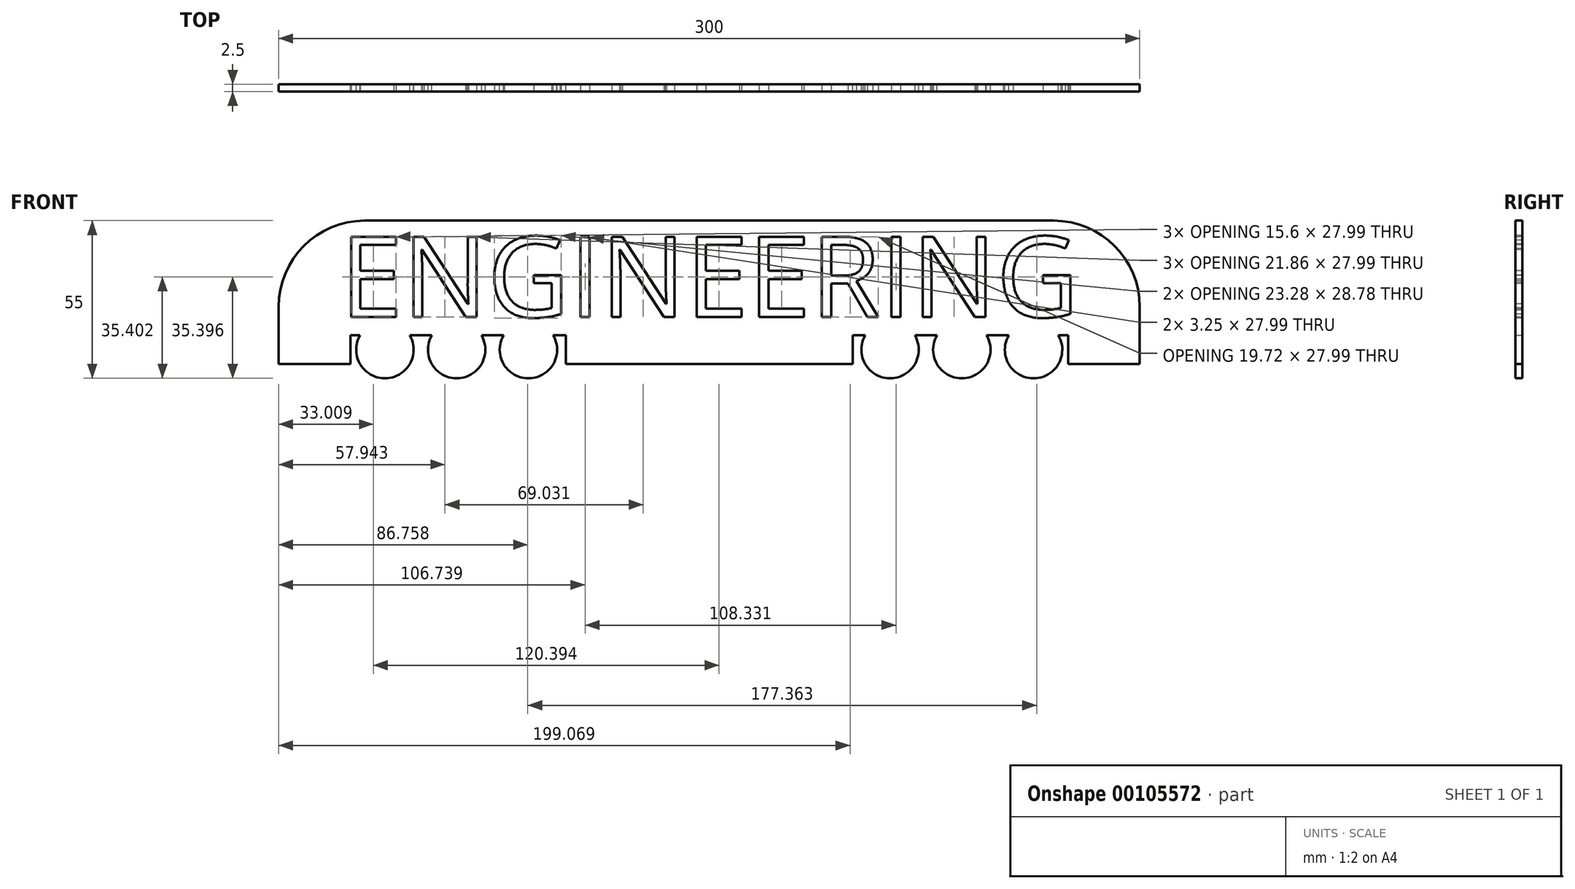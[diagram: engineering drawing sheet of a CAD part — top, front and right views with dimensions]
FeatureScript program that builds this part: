
annotation { "Feature Type Name" : "Feature", "Feature Type Description" : "" }
export const myFeature = defineFeature(function(context is Context, id is Id, definition is map)
    precondition{}
    {
        {
            var Q0;
            Q0=qCreatedBy(makeId("Front.planeOp"),FACE);
            var sketch = newSketch(context, id + "F0", { "sketchPlane" : qUnion([Q0])});
            skLineSegment(sketch, "E0", {"start": v(0, 0) * mm, "end": v(-50, 0) * mm});
            skLineSegment(sketch, "E1", {"start": v(-50, 0) * mm, "end": v(-50, 10) * mm});
            skLineSegment(sketch, "E2", {"start": v(-50, 10) * mm, "end": v(-54.34, 10) * mm});
            skLineSegment(sketch, "E3", {"start": v(-125, 10) * mm, "end": v(-125, 0) * mm});
            skLineSegment(sketch, "E4", {"start": v(-125, 0) * mm, "end": v(-150, 0) * mm});
            skLineSegment(sketch, "E5", {"start": v(-150, 0) * mm, "end": v(-150, 20) * mm});
            skLineSegment(sketch, "E6", {"start": v(-120, 50) * mm, "end": v(0, 50) * mm});
            skLineSegment(sketch, "E7", {"start": v(0, 50) * mm, "end": v(0, 0) * mm, "construction": true});
            skPoint(sketch, "E8.visualSharp", {"position": v(-150, 50) * mm});
            skArc(sketch, "E8.filletArc", {"start": v(-120, 50) * mm, "mid": v(-141.21, 41.21) * mm, "end": v(-150, 20) * mm});
            skArc(sketch, "E9", {"start": v(-121.66, 10) * mm, "mid": v(-113, -5) * mm, "end": v(-104.34, 10) * mm});
            skArc(sketch, "E10.1.0.0", {"start": v(-96.66, 10) * mm, "mid": v(-88, -5) * mm, "end": v(-79.34, 10) * mm});
            skArc(sketch, "E10.2.0.0", {"start": v(-71.66, 10) * mm, "mid": v(-63, -5) * mm, "end": v(-54.34, 10) * mm});
            skLineSegment(sketch, "E10.direction1", {"start": v(-113, 5) * mm, "end": v(-88, 5) * mm, "construction": true});
            skLineSegment(sketch, "E11.trimOffspring", {"start": v(-121.66, 10) * mm, "end": v(-125, 10) * mm});
            skLineSegment(sketch, "E12.trimOffspring", {"start": v(-96.66, 10) * mm, "end": v(-104.34, 10) * mm});
            skLineSegment(sketch, "E13.trimOffspring", {"start": v(-71.66, 10) * mm, "end": v(-79.34, 10) * mm});
            skLineSegment(sketch, "E14.MirrorCS", {"start": v(120, 50) * mm, "end": v(0, 50) * mm});
            skArc(sketch, "E15.MirrorCS", {"start": v(120, 50) * mm, "mid": v(141.21, 41.21) * mm, "end": v(150, 20) * mm});
            skLineSegment(sketch, "E16.MirrorCS", {"start": v(150, 0) * mm, "end": v(150, 20) * mm});
            skLineSegment(sketch, "E17.MirrorCS", {"start": v(125, 0) * mm, "end": v(150, 0) * mm});
            skLineSegment(sketch, "E18.MirrorCS", {"start": v(125, 10) * mm, "end": v(125, 0) * mm});
            skLineSegment(sketch, "E19.MirrorCS", {"start": v(121.66, 10) * mm, "end": v(125, 10) * mm});
            skArc(sketch, "E20.MirrorCS", {"start": v(121.66, 10) * mm, "mid": v(113, -5) * mm, "end": v(104.34, 10) * mm});
            skLineSegment(sketch, "E21.MirrorCS", {"start": v(96.66, 10) * mm, "end": v(104.34, 10) * mm});
            skArc(sketch, "E22.MirrorCS", {"start": v(96.66, 10) * mm, "mid": v(88, -5) * mm, "end": v(79.34, 10) * mm});
            skLineSegment(sketch, "E23.MirrorCS", {"start": v(71.66, 10) * mm, "end": v(79.34, 10) * mm});
            skArc(sketch, "E24.MirrorCS", {"start": v(71.66, 10) * mm, "mid": v(63, -5) * mm, "end": v(54.34, 10) * mm});
            skLineSegment(sketch, "E25.MirrorCS", {"start": v(50, 10) * mm, "end": v(54.34, 10) * mm});
            skLineSegment(sketch, "E26.MirrorCS", {"start": v(50, 0) * mm, "end": v(50, 10) * mm});
            skLineSegment(sketch, "E27.MirrorCS", {"start": v(0, 0) * mm, "end": v(50, 0) * mm});
            skSolve(sketch);
        }
        {
            var Q0;
            Q0=qCreatedBy(makeId("Front.planeOp"),FACE);
            var sketch = newSketch(context, id + "F1", { "sketchPlane" : qUnion([Q0])});
            skText(sketch, "E28", { "text": "ENGINEERING", "fontName": "OpenSans-Regular.ttf"});
            const initialGuessF1  = {"E28": [-0.12864, 0.0164, 1, 0, 0.02823]};
            skSetInitialGuess(sketch, initialGuessF1);
            skSolve(sketch);
        }
        {
            var Q0;
            Q0=makeQuery(id+"F0.imprint","IMPRINT",FACE,{"disambiguationData":[TD([[makeQuery(id+"F0.imprint","IMPRINT",EDGE,{"derivedFrom":sQuery(id+"F0.wireOp",EDGE,"E0")}),-1.0]])]});
            extrude(context, id + "F2", {"entities" : qUnion([Q0]), "depth" : 5 * mm, "symmetric" : true});
        }
        {
            var Q0;
            Q0 = qSketchRegion(id + "F1", true);
            var Q1;
            Q1=makeQuery(id+"F2.opExtrude","CAP_FACE",FACE,{"disambiguationData":[OSD([sQuery(id+"F0.wireOp",EDGE,"E0"),sQuery(id+"F0.wireOp",EDGE,"E1"),sQuery(id+"F0.wireOp",EDGE,"E2"),sQuery(id+"F0.wireOp",EDGE,"E3"),sQuery(id+"F0.wireOp",EDGE,"E4"),sQuery(id+"F0.wireOp",EDGE,"E5"),sQuery(id+"F0.wireOp",EDGE,"E6"),sQuery(id+"F0.wireOp",EDGE,"E8.filletArc"),sQuery(id+"F0.wireOp",EDGE,"E9"),sQuery(id+"F0.wireOp",EDGE,"E10.1.0.0"),sQuery(id+"F0.wireOp",EDGE,"E10.2.0.0"),sQuery(id+"F0.wireOp",EDGE,"E11.trimOffspring"),sQuery(id+"F0.wireOp",EDGE,"E12.trimOffspring"),sQuery(id+"F0.wireOp",EDGE,"E13.trimOffspring"),sQuery(id+"F0.wireOp",EDGE,"E14.MirrorCS"),sQuery(id+"F0.wireOp",EDGE,"E15.MirrorCS"),sQuery(id+"F0.wireOp",EDGE,"E16.MirrorCS"),sQuery(id+"F0.wireOp",EDGE,"E17.MirrorCS"),sQuery(id+"F0.wireOp",EDGE,"E18.MirrorCS"),sQuery(id+"F0.wireOp",EDGE,"E19.MirrorCS"),sQuery(id+"F0.wireOp",EDGE,"E20.MirrorCS"),sQuery(id+"F0.wireOp",EDGE,"E21.MirrorCS"),sQuery(id+"F0.wireOp",EDGE,"E22.MirrorCS"),sQuery(id+"F0.wireOp",EDGE,"E23.MirrorCS"),sQuery(id+"F0.wireOp",EDGE,"E24.MirrorCS"),sQuery(id+"F0.wireOp",EDGE,"E25.MirrorCS"),sQuery(id+"F0.wireOp",EDGE,"E26.MirrorCS"),sQuery(id+"F0.wireOp",EDGE,"E27.MirrorCS")])],"isStart":false});
            extrude(context, id + "F3", {"entities" : qUnion([Q0, Q1]), "operationType" : NewBodyOperationType.REMOVE, "oppositeDirection" : true, "depth" : 5 * mm, "symmetric" : true});
        }
    });
